# Revit family: Deca_Ducha manual sem registro_Ducha Activa Competitivo_1983.ACT
name_source: partatom
category: Plumbing Fixtures
units: mm (PartAtom-declared; Revit-internal decimal feet)

## family parameters
Cut with Voids When Loaded = No
Host = Face
Part Type = Normal
Room Calculation Point = No
Round Connector Dimension = Use Radius
Shared = No

## types (6) — shared parameters
Acompanha o Produto = Acompanha Deca confort + Parafuso e bucha para fixação + Tampão para louça
Aprovado por = quattroD
Atendimento ao Cliente = 0800-0117073
Categoria = METAIS PARA BANHEIRO
Composição Anel Vedação = -
Composição Assento = -
Composição Básica = Liga cobre (bronze e latão),Aço,Plástico de Engenharia,Elastômeros
Composição Componente = -
Consumo = -
Cor Interna = -
Cores Componente = -
Criado por = quattroD
Código Pai = 1983.ACT
Description = Ducha manual sem registro
Diâmetro Água Fria = 0.02 m
Informações Complementares = -
Itens de Instalação = -
Linha = Ducha Activa Competitivo
Manufacturer = Deca
Norma = NBR14877
Pressão máx. funcionamento = 40 MCA
Pressão mín. Aquec. Acúmulo = -
Pressão mín. Aquec. Passagem = -
Pressão mín. funcionamento = 2 MCA
Raio Água Fria = 0.01 m
Saída de Esgoto = -
Segmento = Banheiro Competitivo
Tipo de dispositivo economizador = Sim
Tipo de mecanismo utilizado = -
Tipo de rosca de entrada = BSP NBR 8133
Tipo de rosca de saída = -
URL = www.deca.com.br
Vazão na Pressão máx. (L/min) = 6
Vazão na Pressão mín. (L/min) = 4
zero-valued in all types: Default Elevation

## per-type parameters (varying)
| type | Cor Principal | Cor Secundária | Material | Material Secundário | Model | Peso Líquido (Kg) |
| 1983.BL.ACT.MT_Black Matte | Black Matte | - | Deca_Black Matte | Deca_Black Matte | 1983.BL.ACT.MT | 0.806 |
| 1983.BL.ACT.NO_Black Noir | Black Noir | - | Deca_Black Noir | Deca_Black Noir | 1983.BL.ACT.NO | 0.806 |
| 1983.CT.ACT.MT_Corten | Corten | Branco | Deca_Corten | Deca_Plástico - Branco | 1983.CT.ACT.MT | 0.956 |
| 1983.GL.ACT_Gold | Gold | Branco | Deca_Gold | Deca_Plástico - Branco | 1983.GL.ACT | 0.805 |
| 1983.GL.ACT.MT_Gold Matte | Gold Matte | Branco | Deca_Gold Matte | Deca_Plástico - Branco | 1983.GL.ACT.MT | 0.805 |
| 1983.GL.ACT.RD_Red Gold | Red Gold | Branco | Deca_Red Gold | Deca_Plástico - Branco | 1983.GL.ACT.RD | 0.805 |

note: source unit labels omitted for Vazão na Pressão máx. (L/min), Vazão na Pressão mín. (L/min) — the stored unit's dimension contradicts the parameter name (converter mislabeling)

## geometry (parser evidence)
native form markers: Sweep x1
no freeform markers — native parametric forms only
